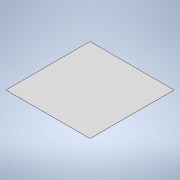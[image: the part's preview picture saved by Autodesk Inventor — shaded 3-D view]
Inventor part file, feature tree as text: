
AUTODESK INVENTOR PART (.ipt)
format: ipt  version: 2021 (Build 250183000, 183)  size: 89,088 bytes
history: native  units: mm
features: extrude x1, sketch x1
ambient origin geometry x8: Origin, YZ Plane, XZ Plane, XY Plane, X Axis, Y Axis, Z Axis, Center Point
bodies: Solid1 (feature_tree)
feature tree (2):
  extrude  "Extrusion1"  Depth=156.5mm
  sketch  "Sketch1"  dims[d0=156.5mm d1=156.5mm d2=0.23mm d3=0.0mm]
